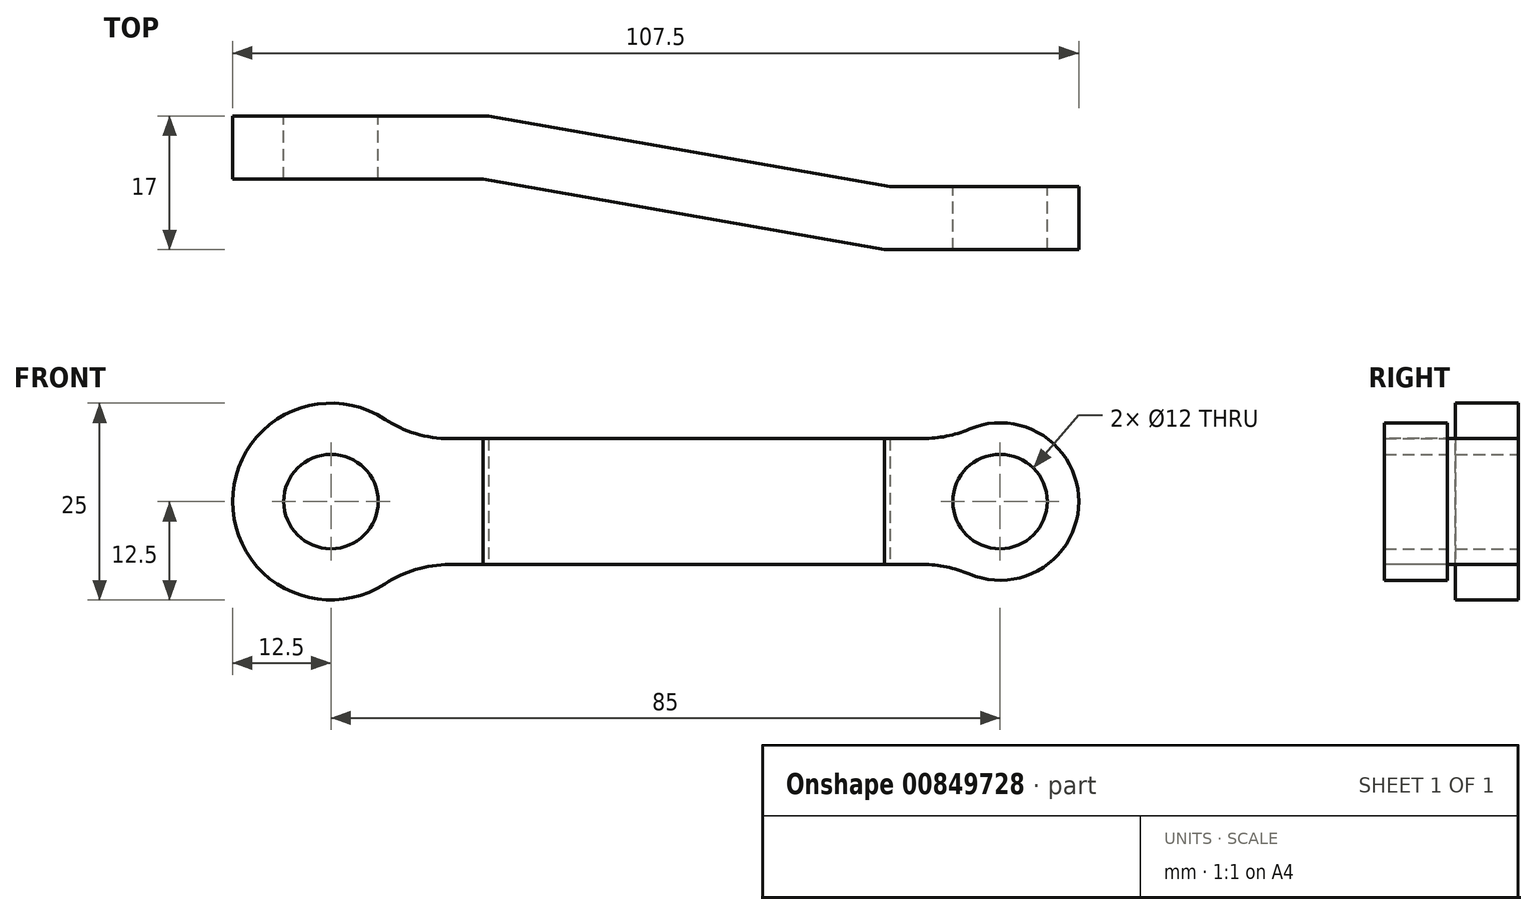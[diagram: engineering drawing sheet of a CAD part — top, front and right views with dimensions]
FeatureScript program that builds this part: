
annotation { "Feature Type Name" : "Feature", "Feature Type Description" : "" }
export const myFeature = defineFeature(function(context is Context, id is Id, definition is map)
    precondition{}
    {
        {
            var Q0;
            Q0=qCreatedBy(makeId("Front.planeOp"),FACE);
            var sketch = newSketch(context, id + "F0", { "sketchPlane" : qUnion([Q0])});
            skCircle(sketch, "E0", {"center": v(0, 0) * mm, "radius": 12.5 * mm});
            skCircle(sketch, "E1", {"center": v(85, 0) * mm, "radius": 10 * mm});
            skLineSegment(sketch, "E2", {"start": v(9.6, 8) * mm, "end": v(79, 8) * mm});
            skLineSegment(sketch, "E3.MirrorCS", {"start": v(9.6, -8) * mm, "end": v(79, -8) * mm});
            skCircle(sketch, "E4", {"center": v(0, 0) * mm, "radius": 6 * mm});
            skCircle(sketch, "E5", {"center": v(85, 0) * mm, "radius": 6 * mm});
            skSolve(sketch);
        }
        {
            var Q0;
            Q0 = qSketchRegion(id + "F0", true);
            extrude(context, id + "F1", {"entities" : qUnion([Q0]), "depth" : 25 * mm, "offsetDistance" : 25 * mm});
        }
        {
            var Q0;
            Q0=qCreatedBy(makeId("Top.planeOp"),FACE);
            var sketch = newSketch(context, id + "F2", { "sketchPlane" : qUnion([Q0])});
            skLineSegment(sketch, "E6", {"start": v(-12.5, 0) * mm, "end": v(20, 0) * mm});
            skLineSegment(sketch, "E7", {"start": v(71.04, -9) * mm, "end": v(20, 0) * mm});
            skLineSegment(sketch, "E8", {"start": v(71.04, -9) * mm, "end": v(95, -9) * mm});
            skLineSegment(sketch, "E9.0", {"start": v(70.34, -17) * mm, "end": v(95, -17) * mm});
            skLineSegment(sketch, "E9.1", {"start": v(70.34, -17) * mm, "end": v(19.3, -8) * mm});
            skLineSegment(sketch, "E9.2", {"start": v(-12.5, -8) * mm, "end": v(19.3, -8) * mm});
            skLineSegment(sketch, "E10", {"start": v(95, -17) * mm, "end": v(95, -9) * mm});
            skLineSegment(sketch, "E11", {"start": v(-12.5, -8) * mm, "end": v(-12.5, 0) * mm});
            skLineSegment(sketch, "E12", {"start": v(95, 0) * mm, "end": v(95, -25) * mm});
            skLineSegment(sketch, "E13", {"start": v(-12.5, -25) * mm, "end": v(-12.5, 0) * mm});
            skSolve(sketch);
        }
        {
            var Q0;
            Q0=makeQuery(id+"F2.imprint","IMPRINT",FACE,{"disambiguationData":[TD([[makeQuery(id+"F2.imprint","IMPRINT",EDGE,{"derivedFrom":sQuery(id+"F2.wireOp",EDGE,"E6")}),-1.0]])]});
            extrude(context, id + "F3", {"entities" : qUnion([Q0]), "operationType" : NewBodyOperationType.INTERSECT, "endBound" : BoundingType.SYMMETRIC, "depth" : 25 * mm, "offsetDistance" : 25 * mm});
        }
        {
            var Q0;
            Q0=makeQuery(id+"F3.boolean.opBoolean","COPY",EDGE,{"derivedFrom":makeQuery(id+"F3.boolean.toolComplement.opBoolean","COPY",EDGE,{"derivedFrom":makeQuery(id+"F3.opExtrude","SWEPT_EDGE",EDGE,{"disambiguationData":[OSD([sQuery(id+"F2.wireOp",EDGE,"E6"),sQuery(id+"F2.wireOp",EDGE,"E7")])]})})});
            var Q1;
            Q1=makeQuery(id+"F3.boolean.opBoolean","COPY",EDGE,{"derivedFrom":makeQuery(id+"F3.boolean.toolComplement.opBoolean","COPY",EDGE,{"derivedFrom":makeQuery(id+"F3.opExtrude","SWEPT_EDGE",EDGE,{"disambiguationData":[OSD([sQuery(id+"F2.wireOp",EDGE,"E9.1"),sQuery(id+"F2.wireOp",EDGE,"E9.2")])]})})});
            var Q2;
            Q2=makeQuery(id+"F3.boolean.opBoolean","COPY",EDGE,{"derivedFrom":makeQuery(id+"F3.boolean.toolComplement.opBoolean","COPY",EDGE,{"derivedFrom":makeQuery(id+"F3.opExtrude","SWEPT_EDGE",EDGE,{"disambiguationData":[OSD([sQuery(id+"F2.wireOp",EDGE,"E9.0"),sQuery(id+"F2.wireOp",EDGE,"E9.1")])]})})});
            var Q3;
            Q3=makeQuery(id+"F3.boolean.opBoolean","COPY",EDGE,{"derivedFrom":makeQuery(id+"F3.boolean.toolComplement.opBoolean","COPY",EDGE,{"derivedFrom":makeQuery(id+"F3.opExtrude","SWEPT_EDGE",EDGE,{"disambiguationData":[OSD([sQuery(id+"F2.wireOp",EDGE,"E7"),sQuery(id+"F2.wireOp",EDGE,"E8")])]})})});
            var Q4;
            Q4=makeQuery(id+"F1.opExtrude","SWEPT_EDGE",EDGE,{"disambiguationData":[OSD([sQuery(id+"F0.wireOp",EDGE,"E1"),sQuery(id+"F0.wireOp",EDGE,"E3.MirrorCS")])]});
            var Q5;
            Q5=makeQuery(id+"F1.opExtrude","SWEPT_EDGE",EDGE,{"disambiguationData":[OSD([sQuery(id+"F0.wireOp",EDGE,"E0"),sQuery(id+"F0.wireOp",EDGE,"E3.MirrorCS")])]});
            var Q6;
            Q6=makeQuery(id+"F1.opExtrude","SWEPT_EDGE",EDGE,{"disambiguationData":[OSD([sQuery(id+"F0.wireOp",EDGE,"E0"),sQuery(id+"F0.wireOp",EDGE,"E2")])]});
            var Q7;
            Q7=makeQuery(id+"F1.opExtrude","SWEPT_EDGE",EDGE,{"disambiguationData":[OSD([sQuery(id+"F0.wireOp",EDGE,"E1"),sQuery(id+"F0.wireOp",EDGE,"E2")])]});
            fillet(context, id + "F4", {"entities" : qUnion([Q0, Q1, Q2, Q3, Q4, Q5, Q6, Q7]), "radius" : 15 * mm, "tangentPropagation" : true, "allowEdgeOverflow" : false});
        }
    });
